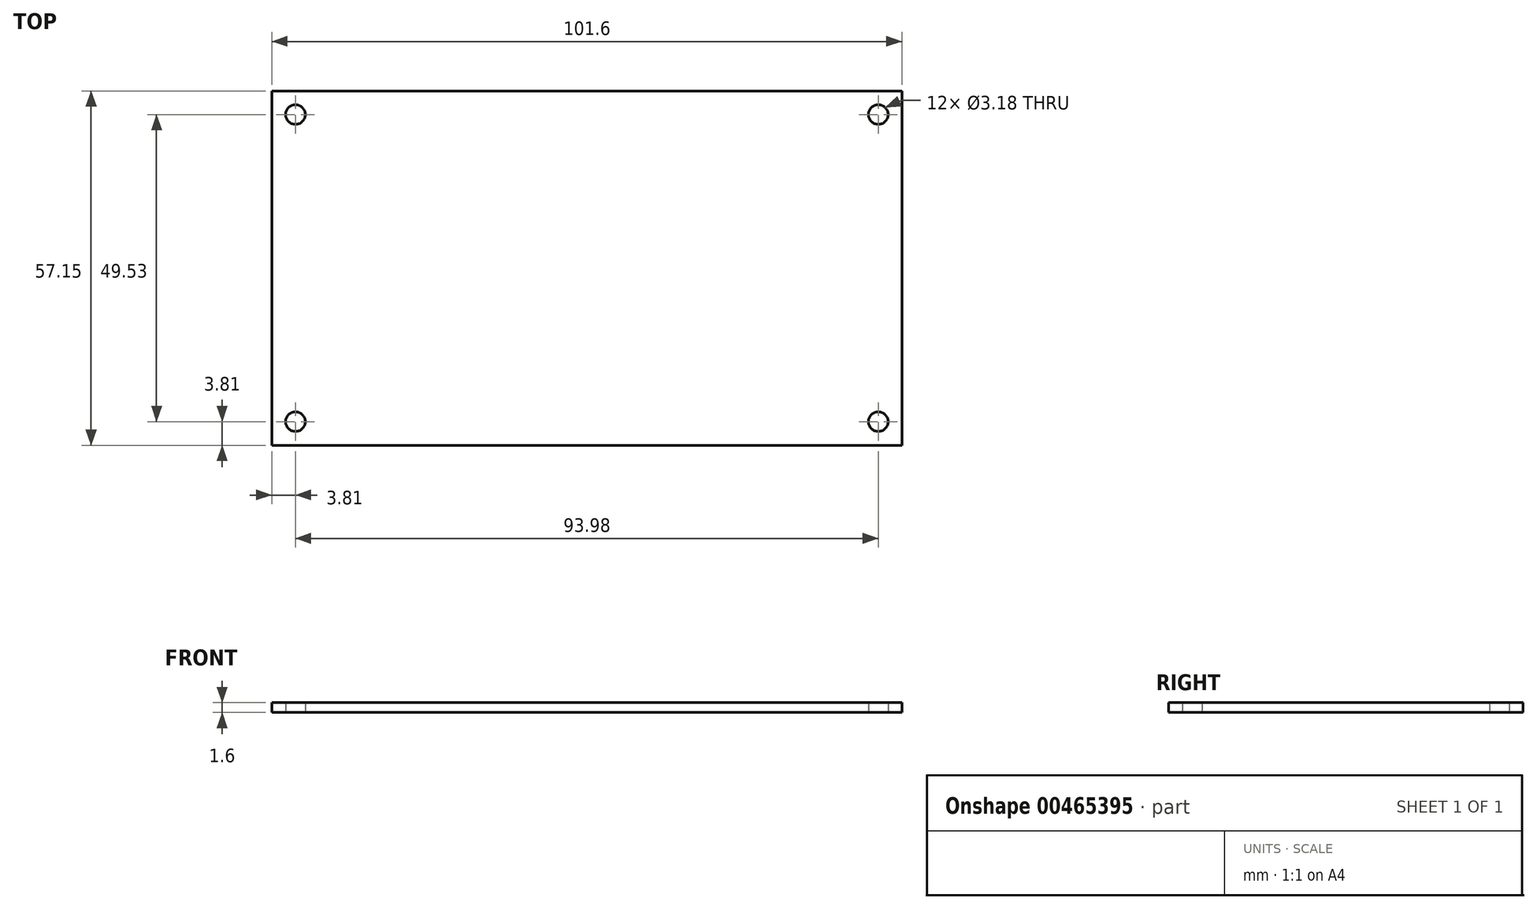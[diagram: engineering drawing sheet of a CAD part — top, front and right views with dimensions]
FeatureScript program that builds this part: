
annotation { "Feature Type Name" : "Feature", "Feature Type Description" : "" }
export const myFeature = defineFeature(function(context is Context, id is Id, definition is map)
    precondition{}
    {
        {
            var Q0;
            Q0=qCreatedBy(makeId("Top.planeOp"),FACE);
            var sketch = newSketch(context, id + "F0", { "sketchPlane" : qUnion([Q0])});
            skLineSegment(sketch, "E0.bottom", {"start": v(0, 0) * mm, "end": v(101.6, 0) * mm});
            skLineSegment(sketch, "E0.top", {"start": v(0, -57.15) * mm, "end": v(101.6, -57.15) * mm});
            skLineSegment(sketch, "E0.left", {"start": v(0, 0) * mm, "end": v(0, -57.15) * mm});
            skLineSegment(sketch, "E0.right", {"start": v(101.6, 0) * mm, "end": v(101.6, -57.15) * mm});
            skCircle(sketch, "E1", {"center": v(3.8, -3.81) * mm, "radius": 1.6 * mm});
            skCircle(sketch, "E2", {"center": v(97.8, -3.81) * mm, "radius": 1.59 * mm});
            skCircle(sketch, "E3", {"center": v(97.8, -53.34) * mm, "radius": 1.6 * mm});
            skCircle(sketch, "E4", {"center": v(3.8, -53.34) * mm, "radius": 1.59 * mm});
            skLineSegment(sketch, "E5", {"start": v(3.8, -3.81) * mm, "end": v(97.8, -3.81) * mm, "construction": true});
            skLineSegment(sketch, "E6", {"start": v(97.8, -3.81) * mm, "end": v(97.8, -53.34) * mm, "construction": true});
            skLineSegment(sketch, "E7", {"start": v(97.8, -53.34) * mm, "end": v(3.8, -53.34) * mm, "construction": true});
            skLineSegment(sketch, "E8", {"start": v(3.8, -3.81) * mm, "end": v(3.8, -53.34) * mm, "construction": true});
            skLineSegment(sketch, "E9", {"start": v(50.8, -57.15) * mm, "end": v(50.8, 0) * mm, "construction": true});
            skPoint(sketch, "E10", {"position": v(50.8, -53.34) * mm});
            skLineSegment(sketch, "E11", {"start": v(0, -28.57) * mm, "end": v(101.6, -28.57) * mm, "construction": true});
            skPoint(sketch, "E12", {"position": v(97.8, -28.57) * mm});
            skSolve(sketch);
        }
        {
            var Q0;
            Q0=makeQuery(id+"F0.imprint","IMPRINT",FACE,{"disambiguationData":[TD([[makeQuery(id+"F0.imprint","IMPRINT",EDGE,{"derivedFrom":sQuery(id+"F0.wireOp",EDGE,"E0.bottom")}),-1.0]])]});
            extrude(context, id + "F1", {"entities" : qUnion([Q0]), "depth" : 1.6 * mm, "offsetDistance" : 25 * mm});
        }
        {
            var Q0;
            Q0=makeQuery(id+"F1.opExtrude","CAP_FACE",FACE,{"disambiguationData":[OSD([sQuery(id+"F0.wireOp",EDGE,"E0.bottom"),sQuery(id+"F0.wireOp",EDGE,"E0.top"),sQuery(id+"F0.wireOp",EDGE,"E0.left"),sQuery(id+"F0.wireOp",EDGE,"E0.right"),sQuery(id+"F0.wireOp",EDGE,"E1"),sQuery(id+"F0.wireOp",EDGE,"E2"),sQuery(id+"F0.wireOp",EDGE,"E3"),sQuery(id+"F0.wireOp",EDGE,"E4")])],"isStart":true});
            var sketch = newSketch(context, id + "F2", { "sketchPlane" : qUnion([Q0])});
            skLineSegment(sketch, "E13", {"start": v(50.8, 0) * mm, "end": v(50.8, 57.15) * mm, "construction": true});
            skPoint(sketch, "E14", {"position": v(50.8, 6.35) * mm});
            skPoint(sketch, "E15", {"position": v(50.8, 50.8) * mm});
            skSolve(sketch);
        }
        {
            var Q0;
            Q0=makeQuery(id+"F1.opExtrude","CAP_FACE",FACE,{"disambiguationData":[OSD([sQuery(id+"F0.wireOp",EDGE,"E0.bottom"),sQuery(id+"F0.wireOp",EDGE,"E0.top"),sQuery(id+"F0.wireOp",EDGE,"E0.left"),sQuery(id+"F0.wireOp",EDGE,"E0.right"),sQuery(id+"F0.wireOp",EDGE,"E1"),sQuery(id+"F0.wireOp",EDGE,"E2"),sQuery(id+"F0.wireOp",EDGE,"E3"),sQuery(id+"F0.wireOp",EDGE,"E4")])],"isStart":false});
            var sketch = newSketch(context, id + "F3", { "sketchPlane" : qUnion([Q0])});
            skLineSegment(sketch, "E16", {"start": v(50.8, -57.15) * mm, "end": v(50.8, 0) * mm});
            skPoint(sketch, "E17", {"position": v(50.8, -6.35) * mm});
            skPoint(sketch, "E18", {"position": v(50.8, -50.8) * mm});
            skSolve(sketch);
        }
    });
